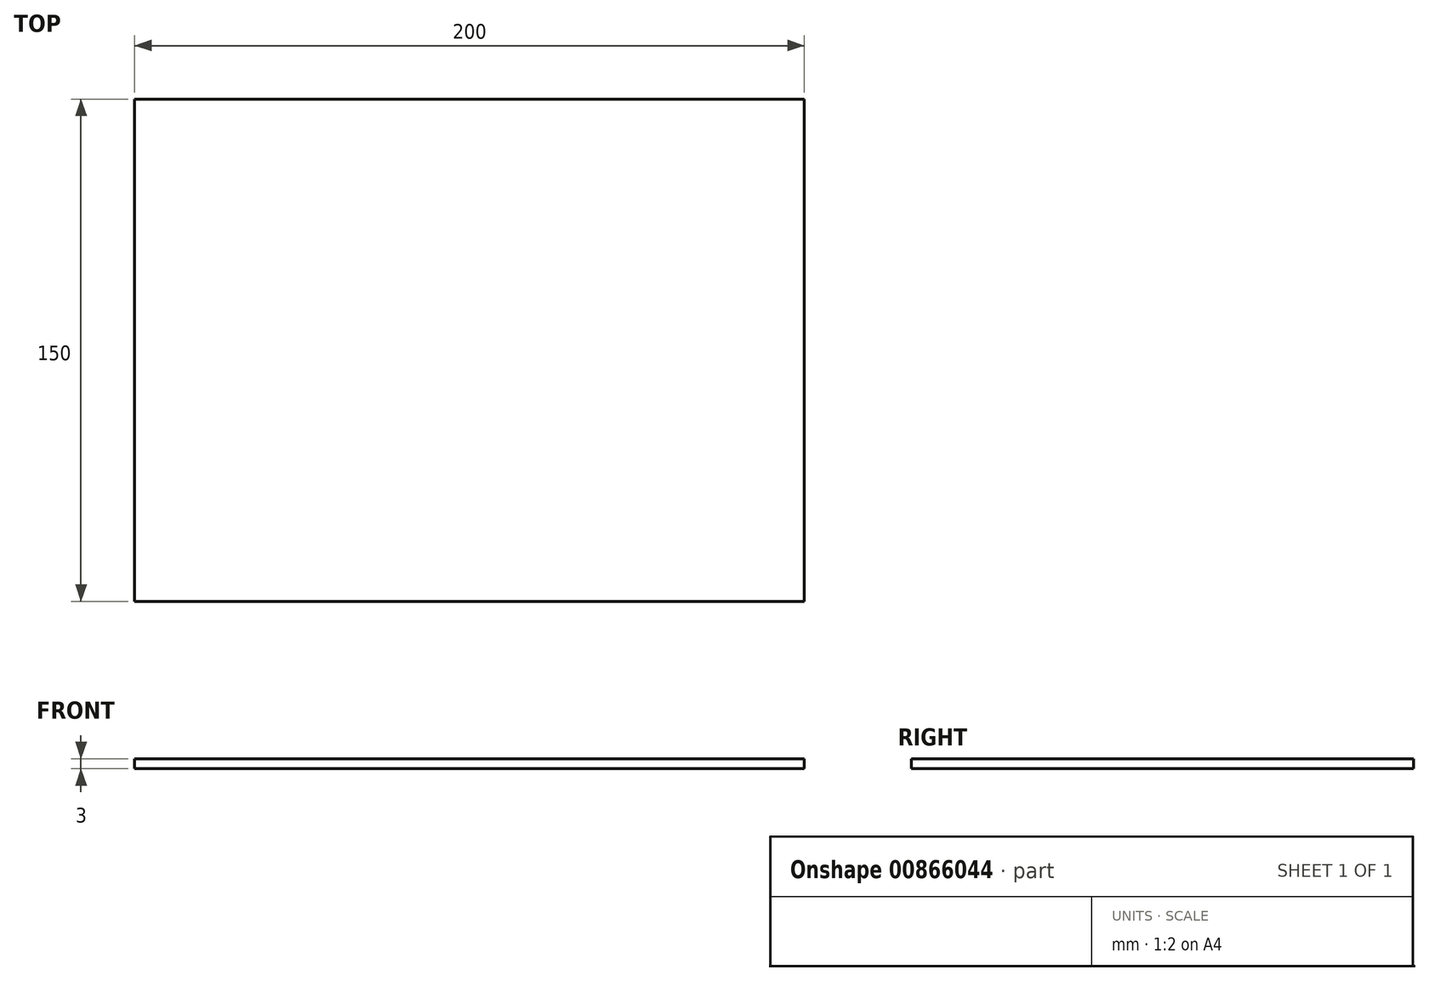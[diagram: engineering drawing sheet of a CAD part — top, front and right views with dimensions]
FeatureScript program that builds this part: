
annotation { "Feature Type Name" : "Feature", "Feature Type Description" : "" }
export const myFeature = defineFeature(function(context is Context, id is Id, definition is map)
    precondition{}
    {
        {
            var Q0;
            Q0=qCreatedBy(makeId("Top.planeOp"),FACE);
            var sketch = newSketch(context, id + "F0", { "sketchPlane" : qUnion([Q0])});
            skLineSegment(sketch, "E0.bottom", {"start": v(100, 75) * mm, "end": v(-100, 75) * mm});
            skLineSegment(sketch, "E0.top", {"start": v(100, -75) * mm, "end": v(-100, -75) * mm});
            skLineSegment(sketch, "E0.left", {"start": v(100, 75) * mm, "end": v(100, -75) * mm});
            skLineSegment(sketch, "E0.right", {"start": v(-100, 75) * mm, "end": v(-100, -75) * mm});
            skPoint(sketch, "E0.middle", {"position": v(0, 0) * mm});
            skSolve(sketch);
        }
        {
            var Q0;
            Q0 = qSketchRegion(id + "F0", true);
            extrude(context, id + "F1", {"entities" : qUnion([Q0]), "depth" : 3 * mm, "offsetDistance" : 25.4 * mm});
        }
    });
